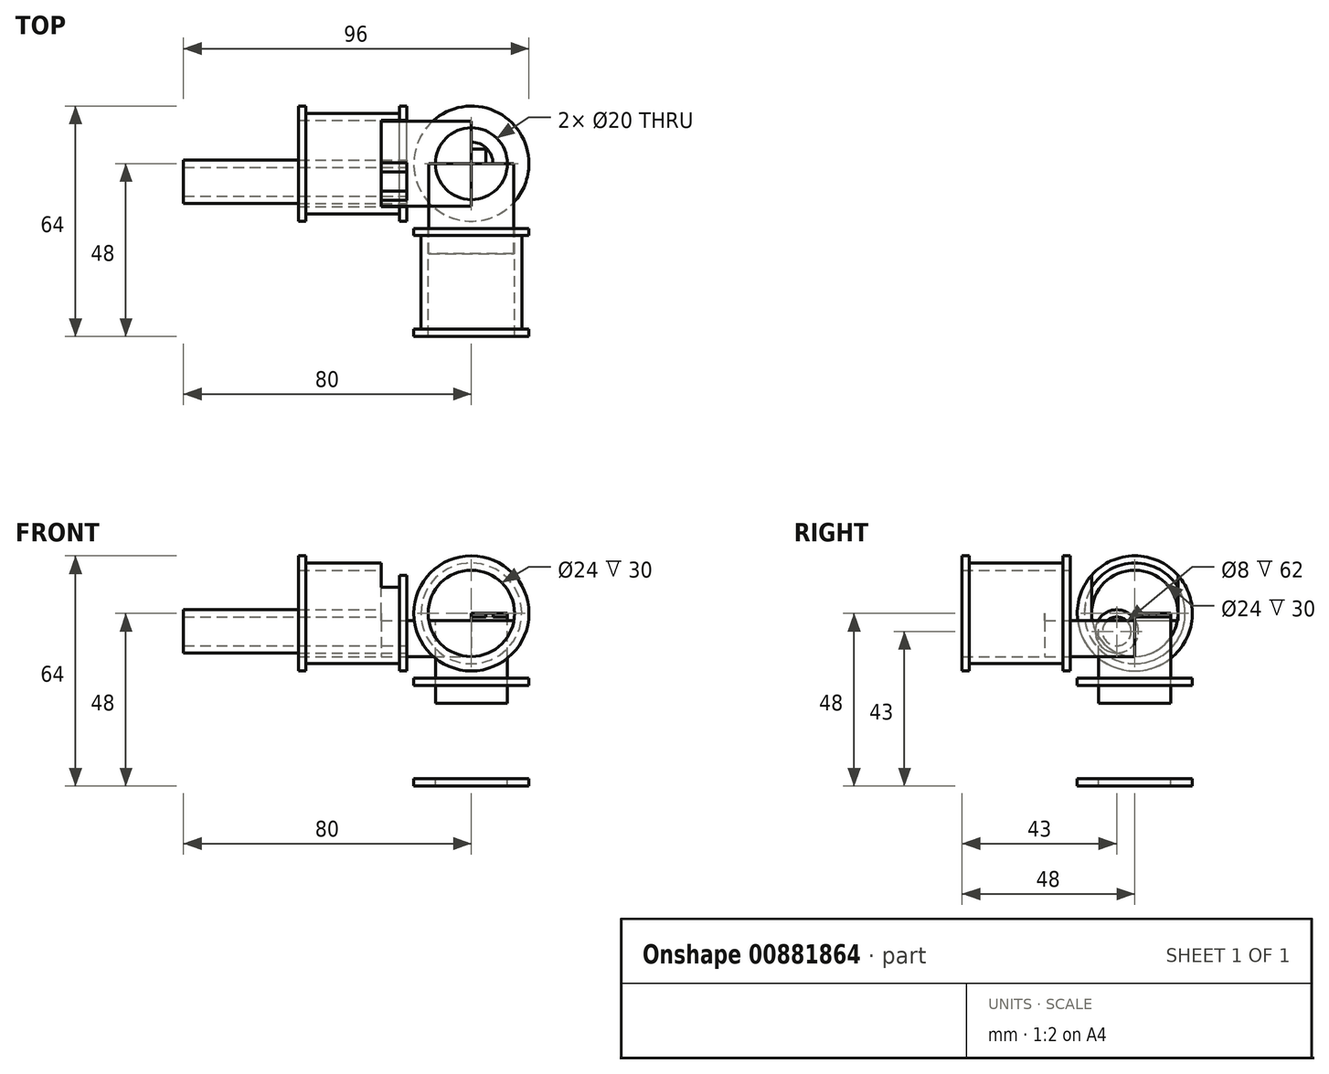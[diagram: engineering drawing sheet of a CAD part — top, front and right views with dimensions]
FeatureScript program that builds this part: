
annotation { "Feature Type Name" : "Feature", "Feature Type Description" : "" }
export const myFeature = defineFeature(function(context is Context, id is Id, definition is map)
    precondition{}
    {
        {
            var Q0;
            Q0=qCreatedBy(makeId("Top.planeOp"),FACE);
            var sketch = newSketch(context, id + "F0", { "sketchPlane" : qUnion([Q0])});
            skLineSegment(sketch, "E0.bottom", {"start": v(4, 4) * mm, "end": v(-4, 4) * mm});
            skLineSegment(sketch, "E0.top", {"start": v(4, -4) * mm, "end": v(-4, -4) * mm});
            skLineSegment(sketch, "E0.left", {"start": v(4, 4) * mm, "end": v(4, -4) * mm});
            skLineSegment(sketch, "E0.right", {"start": v(-4, 4) * mm, "end": v(-4, -4) * mm});
            skPoint(sketch, "E0.middle", {"position": v(0, 0) * mm});
            skCircle(sketch, "E1", {"center": v(0, 0) * mm, "radius": 16 * mm});
            skCircle(sketch, "E2", {"center": v(0, 0) * mm, "radius": 10 * mm});
            skCircle(sketch, "E3", {"center": v(0, 0) * mm, "radius": 6 * mm});
            skCircle(sketch, "E4", {"center": v(0, 0) * mm, "radius": 18.5 * mm});
            skSolve(sketch);
        }
        {
            var Q0;
            Q0=qCreatedBy(makeId("Right.planeOp"),FACE);
            var sketch = newSketch(context, id + "F1", { "sketchPlane" : qUnion([Q0])});
            skCircle(sketch, "E5", {"center": v(0, 0) * mm, "radius": 16 * mm});
            skCircle(sketch, "E6", {"center": v(0, 0) * mm, "radius": 14 * mm});
            skCircle(sketch, "E7", {"center": v(0, 0) * mm, "radius": 12 * mm});
            skLineSegment(sketch, "E8", {"start": v(-12, 0) * mm, "end": v(12, 0) * mm});
            skSolve(sketch);
        }
        {
            var Q0;
            Q0=qCreatedBy(makeId("Front.planeOp"),FACE);
            var sketch = newSketch(context, id + "F2", { "sketchPlane" : qUnion([Q0])});
            skCircle(sketch, "E9", {"center": v(0, 0) * mm, "radius": 16 * mm});
            skCircle(sketch, "E10", {"center": v(0, 0) * mm, "radius": 14 * mm});
            skCircle(sketch, "E11", {"center": v(0, 0) * mm, "radius": 12 * mm});
            skLineSegment(sketch, "E12", {"start": v(12, 0) * mm, "end": v(-12, 0) * mm});
            skSolve(sketch);
        }
        {
            var Q0;
            Q0=makeQuery(id+"F0.imprint","IMPRINT",FACE,{"disambiguationData":[TD([[makeQuery(id+"F0.imprint","IMPRINT",EDGE,{"derivedFrom":sQuery(id+"F0.wireOp",EDGE,"E1")}),1.0]])]});
            extrude(context, id + "F3", {"entities" : qUnion([Q0]), "oppositeDirection" : true, "depth" : 46 * mm, "offsetDistance" : 25 * mm, "hasSecondDirection" : true, "secondDirectionOppositeDirection" : true, "secondDirectionDepth" : 20 * mm});
        }
        {
            var Q0;
            Q0=makeQuery(id+"F1.imprint","IMPRINT",FACE,{"disambiguationData":[TD([[makeQuery(id+"F1.imprint","IMPRINT",EDGE,{"derivedFrom":sQuery(id+"F1.wireOp",EDGE,"E5")}),1.0]])]});
            extrude(context, id + "F4", {"entities" : qUnion([Q0]), "oppositeDirection" : true, "depth" : 46 * mm, "offsetDistance" : 25 * mm, "hasSecondDirection" : true, "secondDirectionOppositeDirection" : true, "secondDirectionDepth" : 20 * mm});
        }
        {
            var Q0;
            Q0=makeQuery(id+"F2.imprint","IMPRINT",FACE,{"disambiguationData":[TD([[makeQuery(id+"F2.imprint","IMPRINT",EDGE,{"derivedFrom":sQuery(id+"F2.wireOp",EDGE,"E9")}),1.0]])]});
            extrude(context, id + "F5", {"entities" : qUnion([Q0]), "depth" : 46 * mm, "offsetDistance" : 25 * mm, "hasSecondDirection" : true, "secondDirectionOppositeDirection" : false, "secondDirectionDepth" : 20 * mm});
        }
        {
            var Q0;
            Q0=makeQuery(id+"F2.imprint","IMPRINT",FACE,{"disambiguationData":[TD([[makeQuery(id+"F2.imprint","IMPRINT",EDGE,{"derivedFrom":sQuery(id+"F2.wireOp",EDGE,"E10")}),1.0]])]});
            var Q1;
            Q1=makeQuery(id+"F2.imprint","IMPRINT",FACE,{"disambiguationData":[TD([[makeQuery(id+"F2.imprint","IMPRINT",EDGE,{"derivedFrom":sQuery(id+"F2.wireOp",EDGE,"E9")}),1.0]])]});
            extrude(context, id + "F6", {"entities" : qUnion([Q0, Q1]), "depth" : 48 * mm, "offsetDistance" : 25 * mm, "hasSecondDirection" : true, "secondDirectionOppositeDirection" : false, "secondDirectionDepth" : 18 * mm});
        }
        {
            var Q0;
            Q0=makeQuery(id+"F1.imprint","IMPRINT",FACE,{"disambiguationData":[TD([[makeQuery(id+"F1.imprint","IMPRINT",EDGE,{"derivedFrom":sQuery(id+"F1.wireOp",EDGE,"E6")}),1.0]])]});
            var Q1;
            Q1=makeQuery(id+"F1.imprint","IMPRINT",FACE,{"disambiguationData":[TD([[makeQuery(id+"F1.imprint","IMPRINT",EDGE,{"derivedFrom":sQuery(id+"F1.wireOp",EDGE,"E5")}),1.0]])]});
            extrude(context, id + "F7", {"entities" : qUnion([Q0, Q1]), "oppositeDirection" : true, "depth" : 48 * mm, "offsetDistance" : 25 * mm, "hasSecondDirection" : true, "secondDirectionOppositeDirection" : true, "secondDirectionDepth" : 18 * mm});
        }
        {
            var Q0;
            Q0=makeQuery(id+"F0.imprint","IMPRINT",FACE,{"disambiguationData":[TD([[makeQuery(id+"F0.imprint","IMPRINT",EDGE,{"derivedFrom":sQuery(id+"F0.wireOp",EDGE,"ACTGSwJK-rgl8-ZAcZ-apFj-MVZtFFcyx2Qq")}),1.0]])]});
            var Q1;
            Q1=makeQuery(id+"F0.imprint","IMPRINT",FACE,{"disambiguationData":[TD([[makeQuery(id+"F0.imprint","IMPRINT",EDGE,{"derivedFrom":sQuery(id+"F0.wireOp",EDGE,"E1")}),1.0]])]});
            extrude(context, id + "F8", {"entities" : qUnion([Q0, Q1]), "oppositeDirection" : true, "depth" : 48 * mm, "offsetDistance" : 25 * mm, "hasSecondDirection" : true, "secondDirectionOppositeDirection" : true, "secondDirectionDepth" : 18 * mm});
        }
        {
            var Q0;
            Q0=makeQuery(id+"F0.imprint","IMPRINT",FACE,{"disambiguationData":[TD([[makeQuery(id+"F0.imprint","IMPRINT",EDGE,{"derivedFrom":sQuery(id+"F0.wireOp",EDGE,"YIG0J7lI-ZUaQ-ceel-rp2b-WwoC8Ox2qIIC")}),-1.0]])]});
            var Q1;
            Q1=makeQuery(id+"F0.imprint","IMPRINT",FACE,{"disambiguationData":[TD([[makeQuery(id+"F0.imprint","IMPRINT",EDGE,{"derivedFrom":sQuery(id+"F0.wireOp",EDGE,"E0.bottom")}),-1.0]])]});
            var Q2;
            Q2=makeQuery(id+"F0.imprint","IMPRINT",FACE,{"disambiguationData":[TD([[makeQuery(id+"F0.imprint","IMPRINT",EDGE,{"derivedFrom":sQuery(id+"F0.wireOp",EDGE,"E0.bottom")}),1.0]])]});
            var Q3;
            Q3=makeQuery(id+"F0.imprint","IMPRINT",FACE,{"disambiguationData":[TD([[makeQuery(id+"F0.imprint","IMPRINT",EDGE,{"derivedFrom":sQuery(id+"F0.wireOp",EDGE,"E2")}),1.0]])]});
            extrude(context, id + "F9", {"entities" : qUnion([Q0, Q1, Q2, Q3]), "oppositeDirection" : true, "depth" : 25 * mm, "offsetDistance" : 25 * mm});
        }
        {
            var Q0;
            Q0=makeQuery(id+"F0.imprint","IMPRINT",FACE,{"disambiguationData":[TD([[makeQuery(id+"F0.imprint","IMPRINT",EDGE,{"derivedFrom":sQuery(id+"F0.wireOp",EDGE,"E0.bottom")}),1.0]])]});
            var Q1;
            Q1=makeQuery(id+"F0.imprint","IMPRINT",FACE,{"disambiguationData":[TD([[makeQuery(id+"F0.imprint","IMPRINT",EDGE,{"derivedFrom":sQuery(id+"F0.wireOp",EDGE,"E2")}),1.0]])]});
            extrude(context, id + "F10", {"entities" : qUnion([Q0, Q1]), "operationType" : NewBodyOperationType.REMOVE, "oppositeDirection" : true, "depth" : 1 * mm, "offsetDistance" : 25 * mm});
        }
        {
            var Q0;
            Q0=makeQuery(id+"F0.imprint","IMPRINT",FACE,{"disambiguationData":[TD([[makeQuery(id+"F0.imprint","IMPRINT",EDGE,{"derivedFrom":sQuery(id+"F0.wireOp",EDGE,"E2")}),1.0]])]});
            extrude(context, id + "F11", {"entities" : qUnion([Q0]), "oppositeDirection" : true, "depth" : 1 * mm, "offsetDistance" : 25 * mm});
        }
        {
            var Q0;
            {var subQ0=sQuery(id+"F2.wireOp",EDGE,"E12");Q0=makeQuery(id+"F2.imprint","IMPRINT",FACE,{"disambiguationData":[TD([[makeQuery(id+"F2.imprint","IMPRINT",EDGE,{"derivedFrom":subQ0}),1.0]])]});}
            extrude(context, id + "F12", {"entities" : qUnion([Q0]), "depth" : 25 * mm, "offsetDistance" : 25 * mm});
        }
        {
            var Q0;
            Q0=makeQuery(id+"F12.opExtrude","SWEPT_FACE",FACE,{"disambiguationData":[OSD([sQuery(id+"F2.wireOp",EDGE,"E12")])]});
            extrude(context, id + "F13", {"entities" : qUnion([Q0]), "operationType" : NewBodyOperationType.REMOVE, "oppositeDirection" : true, "depth" : 2 * mm, "offsetDistance" : 25 * mm});
        }
        {
            var Q0;
            {var subQ0=sQuery(id+"F1.wireOp",EDGE,"E8");Q0=makeQuery(id+"F1.imprint","IMPRINT",FACE,{"disambiguationData":[TD([[makeQuery(id+"F1.imprint","IMPRINT",EDGE,{"derivedFrom":subQ0}),-1.0]])]});}
            extrude(context, id + "F14", {"entities" : qUnion([Q0]), "oppositeDirection" : true, "depth" : 25 * mm, "offsetDistance" : 25 * mm});
        }
        {
            var Q0;
            Q0=qCreatedBy(makeId("Right.planeOp"),FACE);
            var sketch = newSketch(context, id + "F15", { "sketchPlane" : qUnion([Q0])});
            skCircle(sketch, "E13", {"center": v(-5, -5) * mm, "radius": 6 * mm});
            skCircle(sketch, "E14", {"center": v(-5, -5) * mm, "radius": 4 * mm});
            skSolve(sketch);
        }
        {
            var Q0;
            Q0=qSketchRegion(id+"F15",true);
            var Q1;
            Q1=makeQuery(id+"F15.imprint","IMPRINT",FACE,{"disambiguationData":[TD([[makeQuery(id+"F15.imprint","IMPRINT",EDGE,{"derivedFrom":sQuery(id+"F15.wireOp",EDGE,"E14")}),1.0]])]});
            extrude(context, id + "F16", {"entities" : qUnion([Q0, Q1]), "oppositeDirection" : true, "depth" : 80 * mm, "offsetDistance" : 25 * mm, "hasSecondDirection" : true, "secondDirectionOppositeDirection" : true, "secondDirectionDepth" : 18 * mm});
        }
        {
            var Q0;
            Q0=makeQuery(id+"F14.opExtrude","SWEPT_FACE",FACE,{"disambiguationData":[OSD([sQuery(id+"F1.wireOp",EDGE,"E8")])]});
            extrude(context, id + "F17", {"entities" : qUnion([Q0]), "operationType" : NewBodyOperationType.REMOVE, "oppositeDirection" : true, "depth" : 2 * mm, "offsetDistance" : 25 * mm, "hasSecondDirection" : true, "secondDirectionOppositeDirection" : false, "secondDirectionDepth" : 25 * mm});
        }
        {
            var Q0;
            Q0=makeQuery(id+"F5.opExtrude","SWEPT_BODY",BODY,{"disambiguationData":[OSD([sQuery(id+"F2.wireOp",EDGE,"E9"),sQuery(id+"F2.wireOp",EDGE,"E10")])]});
            var Q1;
            Q1=makeQuery(id+"F6.opExtrude","SWEPT_BODY",BODY,{"disambiguationData":[OSD([sQuery(id+"F2.wireOp",EDGE,"E9"),sQuery(id+"F2.wireOp",EDGE,"E11")])]});
            booleanBodies(context, id + "F18", {"operationType" : BooleanOperationType.SUBTRACTION, "tools" : qUnion([Q0]), "targets" : qUnion([Q1])});
        }
        {
            var Q0;
            Q0=makeQuery(id+"F4.opExtrude","SWEPT_BODY",BODY,{"disambiguationData":[OSD([sQuery(id+"F1.wireOp",EDGE,"E5"),sQuery(id+"F1.wireOp",EDGE,"E6")])]});
            var Q1;
            Q1=makeQuery(id+"F7.opExtrude","SWEPT_BODY",BODY,{"disambiguationData":[OSD([sQuery(id+"F1.wireOp",EDGE,"E5"),sQuery(id+"F1.wireOp",EDGE,"E7")])]});
            booleanBodies(context, id + "F19", {"operationType" : BooleanOperationType.SUBTRACTION, "tools" : qUnion([Q0]), "targets" : qUnion([Q1])});
        }
        {
            var Q0;
            Q0=makeQuery(id+"F3.opExtrude","SWEPT_BODY",BODY,{"disambiguationData":[OSD([sQuery(id+"F0.wireOp",EDGE,"E1"),sQuery(id+"F0.wireOp",EDGE,"ACTGSwJK-rgl8-ZAcZ-apFj-MVZtFFcyx2Qq")])]});
            var Q1;
            Q1=makeQuery(id+"F8.opExtrude","SWEPT_BODY",BODY,{"disambiguationData":[OSD([sQuery(id+"F0.wireOp",EDGE,"E1"),sQuery(id+"F0.wireOp",EDGE,"E2")])]});
            booleanBodies(context, id + "F20", {"operationType" : BooleanOperationType.SUBTRACTION, "tools" : qUnion([Q0]), "targets" : qUnion([Q1])});
        }
        {
            var Q0;
            Q0=makeQuery(id+"F15.imprint","IMPRINT",FACE,{"disambiguationData":[TD([[makeQuery(id+"F15.imprint","IMPRINT",EDGE,{"derivedFrom":sQuery(id+"F15.wireOp",EDGE,"E14")}),1.0]])]});
            extrude(context, id + "F21", {"entities" : qUnion([Q0]), "operationType" : NewBodyOperationType.REMOVE, "oppositeDirection" : true, "depth" : 80 * mm, "offsetDistance" : 25 * mm, "hasSecondDirection" : true, "secondDirectionOppositeDirection" : true, "secondDirectionDepth" : 18 * mm});
        }
    });
